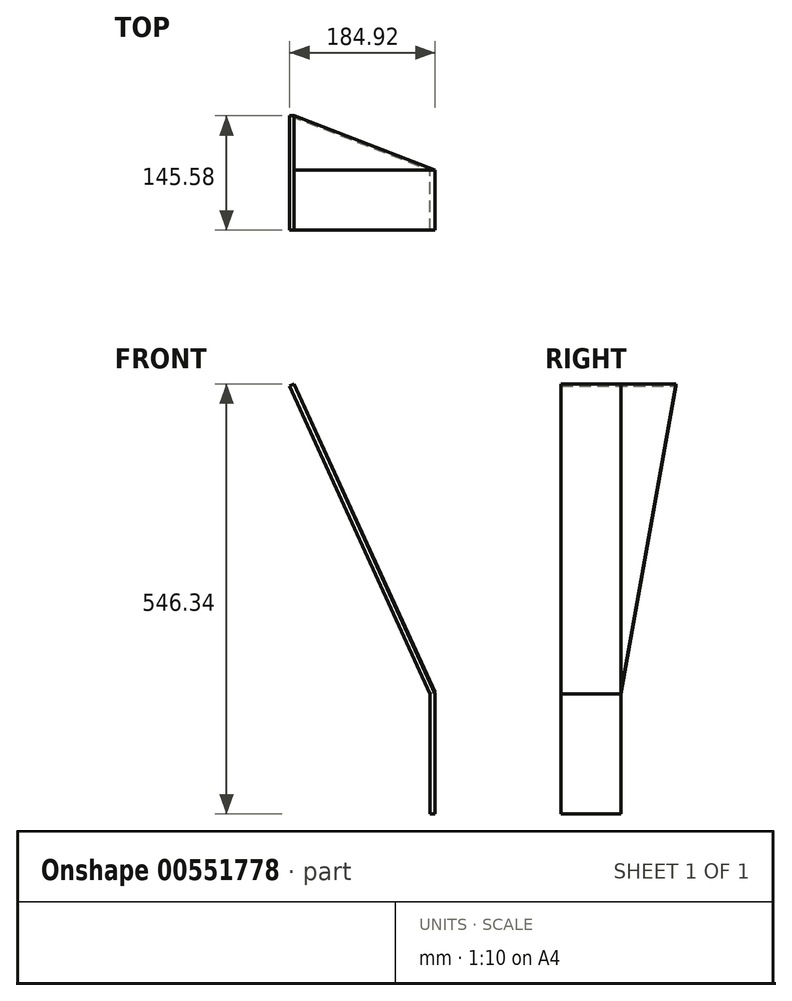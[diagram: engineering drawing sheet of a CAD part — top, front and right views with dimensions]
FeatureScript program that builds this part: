
annotation { "Feature Type Name" : "Feature", "Feature Type Description" : "" }
export const myFeature = defineFeature(function(context is Context, id is Id, definition is map)
    precondition{}
    {
        {
            var Q0;
            Q0=qCreatedBy(makeId("Front.planeOp"),FACE);
            var sketch = newSketch(context, id + "F0", { "sketchPlane" : qUnion([Q0])});
            skLineSegment(sketch, "E0", {"start": v(6.35, 0) * mm, "end": v(6.35, 76.2) * mm});
            skLineSegment(sketch, "E1", {"start": v(0, 76.2) * mm, "end": v(0, 0) * mm});
            skLineSegment(sketch, "E2", {"start": v(6.35, 76.2) * mm, "end": v(-173.32, 469.9) * mm});
            skLineSegment(sketch, "E3", {"start": v(0, 0) * mm, "end": v(0, -76.2) * mm});
            skLineSegment(sketch, "E4", {"start": v(0, -76.2) * mm, "end": v(6.35, -76.2) * mm});
            skLineSegment(sketch, "E5", {"start": v(6.35, -76.2) * mm, "end": v(6.35, 0) * mm});
            skLineSegment(sketch, "E6", {"start": v(-173.32, 469.9) * mm, "end": v(-178.57, 467.5) * mm});
            skLineSegment(sketch, "E7", {"start": v(0, 76.2) * mm, "end": v(-178.57, 467.5) * mm});
            skSolve(sketch);
        }
        {
            var Q0;
            Q0=makeQuery(id+"F0.imprint","IMPRINT",FACE,{"disambiguationData":[TD([[makeQuery(id+"F0.imprint","IMPRINT",EDGE,{"derivedFrom":sQuery(id+"F0.wireOp",EDGE,"E0")}),1.0]])]});
            extrude(context, id + "F1", {"entities" : qUnion([Q0]), "depth" : 76.2 * mm, "offsetDistance" : 25.4 * mm});
        }
        {
            var Q0;
            Q0=makeQuery(id+"F1.opExtrude","SWEPT_FACE",FACE,{"disambiguationData":[OSD([sQuery(id+"F0.wireOp",EDGE,"E7")])]});
            var sketch = newSketch(context, id + "F2", { "sketchPlane" : qUnion([Q0])});
            skLineSegment(sketch, "E8", {"start": v(0, 499.45) * mm, "end": v(-69.38, 499.45) * mm});
            skLineSegment(sketch, "E9", {"start": v(-69.38, 499.45) * mm, "end": v(0, 69.32) * mm});
            skSolve(sketch);
        }
        {
            var Q0;
            Q0=makeQuery(id+"F2.imprint","IMPRINT",FACE,{"disambiguationData":[TD([[makeQuery(id+"F2.imprint","IMPRINT",EDGE,{"derivedFrom":sQuery(id+"F2.wireOp",EDGE,"E8")}),1.0]])]});
            extrude(context, id + "F3", {"entities" : qUnion([Q0]), "operationType" : NewBodyOperationType.ADD, "oppositeDirection" : true, "depth" : 6.35 * mm, "offsetDistance" : 25.4 * mm});
        }
    });
